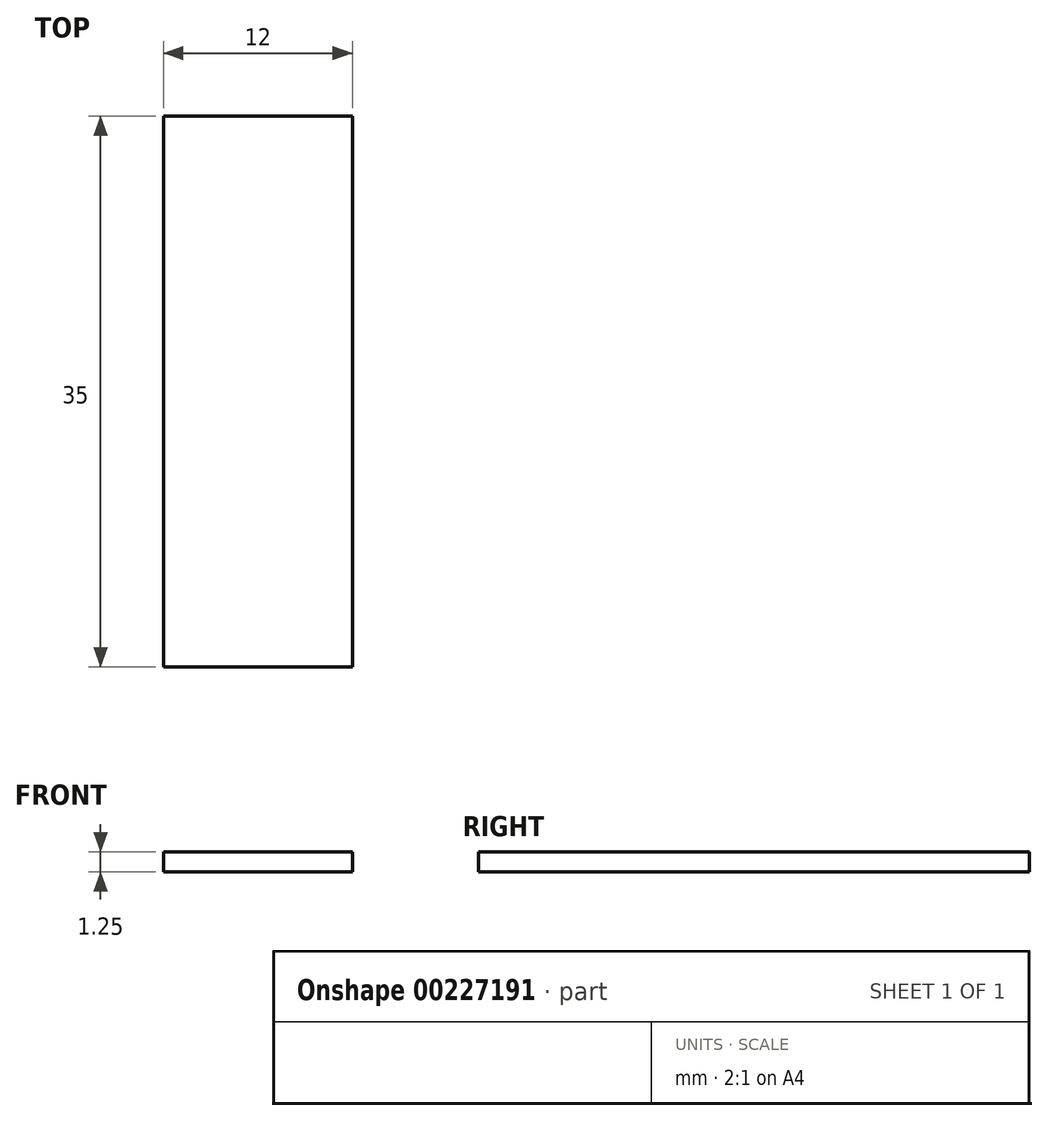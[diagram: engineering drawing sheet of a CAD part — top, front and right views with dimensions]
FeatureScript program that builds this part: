
annotation { "Feature Type Name" : "Feature", "Feature Type Description" : "" }
export const myFeature = defineFeature(function(context is Context, id is Id, definition is map)
    precondition{}
    {
        {
            var Q0;
            Q0=qCreatedBy(makeId("Top.planeOp"),FACE);
            var sketch = newSketch(context, id + "F0", { "sketchPlane" : qUnion([Q0])});
            skLineSegment(sketch, "E0.bottom", {"start": v(-6, 17.5) * mm, "end": v(6, 17.5) * mm});
            skLineSegment(sketch, "E0.top", {"start": v(-6, -17.5) * mm, "end": v(6, -17.5) * mm});
            skLineSegment(sketch, "E0.left", {"start": v(-6, 17.5) * mm, "end": v(-6, -17.5) * mm});
            skLineSegment(sketch, "E0.right", {"start": v(6, 17.5) * mm, "end": v(6, -17.5) * mm});
            skPoint(sketch, "E0.middle", {"position": v(0, 0) * mm});
            skSolve(sketch);
        }
        {
            var Q0;
            Q0=makeQuery(id+"F0.imprint","IMPRINT",FACE,{"disambiguationData":[TD([[makeQuery(id+"F0.imprint","IMPRINT",EDGE,{"derivedFrom":sQuery(id+"F0.wireOp",EDGE,"E0.bottom")}),-1.0]])]});
            extrude(context, id + "F1", {"entities" : qUnion([Q0]), "depth" : 1.25 * mm});
        }
    });
